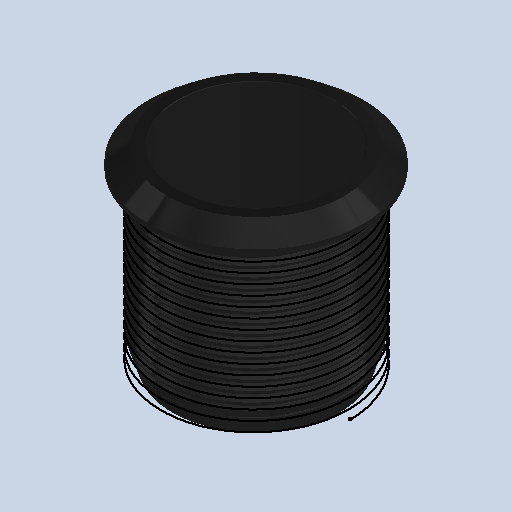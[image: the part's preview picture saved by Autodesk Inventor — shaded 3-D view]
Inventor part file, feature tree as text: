
AUTODESK INVENTOR PART (.ipt)
format: ipt  version: 2022 (Build 260153000, 153)  size: 608,256 bytes
history: mixed  units: mm (DEFAULTED — no unit token found)
features: other x9, sketch x1, chamfer x1, imported_body x1
bodies: Body1 (imported_parasolid)
feature tree (12):
  other  "Sólido1"
  other  "Origen"
  other  "Geometría reparada1"
  other  "Plano YZ"
  other  "Plano XZ"
  other  "Plano XY"
  other  "Eje X"
  other  "Eje Y"
  other  "Eje Z"
  sketch  "Boceto 3D1"
  chamfer  "Chaflán2"  [1 undecoded]
  imported_body  NMx_Import_Brep_tag  [imported B-rep: ~7 faces, bbox_mm=[0.0, 0.0, 0.0]]
note: 1 required parameter value undecoded (feature->parameter linkage not recoverable at this tier; creation-order binding heuristic only, values carry confidence <= 0.55)
